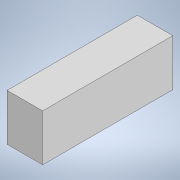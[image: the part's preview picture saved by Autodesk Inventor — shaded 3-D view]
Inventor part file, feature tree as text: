
AUTODESK INVENTOR PART (.ipt)
format: ipt  version: 2022 (Build 260153000, 153)  size: 90,624 bytes
history: native  units: in
note: dims shown in document units (in); Inventor stores cm internally (conversion verified against a paired STEP export)
features: extrude x1, sketch x1
ambient origin geometry x8: Origin, YZ Plane, XZ Plane, XY Plane, X Axis, Y Axis, Z Axis, Center Point
bodies: Solid1 (feature_tree)
feature tree (2):
  extrude  "Extrusion1"  Depth=0.0866in
  sketch  "Sketch1"  dims[d0=0.0236in d1=0.0866in d2=0.0311in d3=0.0in]
